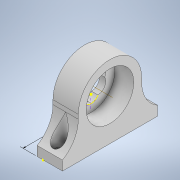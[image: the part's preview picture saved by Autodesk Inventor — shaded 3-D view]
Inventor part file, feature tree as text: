
AUTODESK INVENTOR PART (.ipt)
format: ipt  version: 2020 (Build 240168000, 168)  size: 207,360 bytes
history: native  units: in
note: dims shown in document units (in); Inventor stores cm internally (conversion verified against a paired STEP export)
features: sketch x8, extrude x5, other x4, fillet x3, pattern_circular x1, hole x1
ambient origin geometry x8: Origin, YZ Plane, XZ Plane, XY Plane, X Axis, Y Axis, Z Axis, Center Point
bodies: Solid1 (feature_tree)
feature tree (22):
  other  "Annotations"
  extrude  "Extrusion1"  Depth=3.0in
  extrude  "Extrusion2"  Depth=0.5in
  extrude  "Extrusion3"  Depth=2.0in TaperAngle=0.0deg
  extrude  "Extrusion4"  Depth=1.0in
  sketch  "Sketch5"  dims[d10=0.6in d11=0.0in]
  other  "Work Axis1"
  pattern_circular  "Circular Pattern1"  [2 undecoded]
  fillet  "Fillet1"  Radius=2.3622in
  fillet  "Fillet2"  Radius=1.0in
  sketch  "Sketch6"  dims[d12=0.25in]
  fillet  "Fillet5"  Radius=1.0in
  hole  "Hole1"  [1 undecoded]
  extrude  "Extrusion5"  Depth=0.2in
  sketch  "Sketch9"  dims[d14=0.5in d15=0.2in d16=0.0in d17=2.3622in d18=360.0deg d20=1.0in d21=1.0in d24=0.4in d25=0.2in d26=0.2in d27=0.2in d28=0.2in d29=1.0in d30=0.2in d31=0.75in d32=0.4in d33=0.15in d34=0.5635in d35=1.0in d36=0.8108in d37=0.4in d38=0.4in d39=1.0in d40=0.0in d41=0.2343in d42=0.2161in d43=3.0in d44=1.0in]
  sketch  "Sketch1"  dims[d0=0.8in d1=3.0in]
  sketch  "Sketch2"  dims[d2=0.3in d3=0.0in d4=0.5in]
  sketch  "Sketch3"  dims[d5=2.0in d6=2.0in d7=0.0in]
  sketch  "Sketch4"  dims[d8=1.0in d9=1.5in]
  sketch  "Sketch8"  dims[d13=0.25in]
  other  "Linear Dimension 1"
  other  "Linear Dimension 2"
note: 3 required parameter values undecoded (feature->parameter linkage not recoverable at this tier; creation-order binding heuristic only, values carry confidence <= 0.55)
